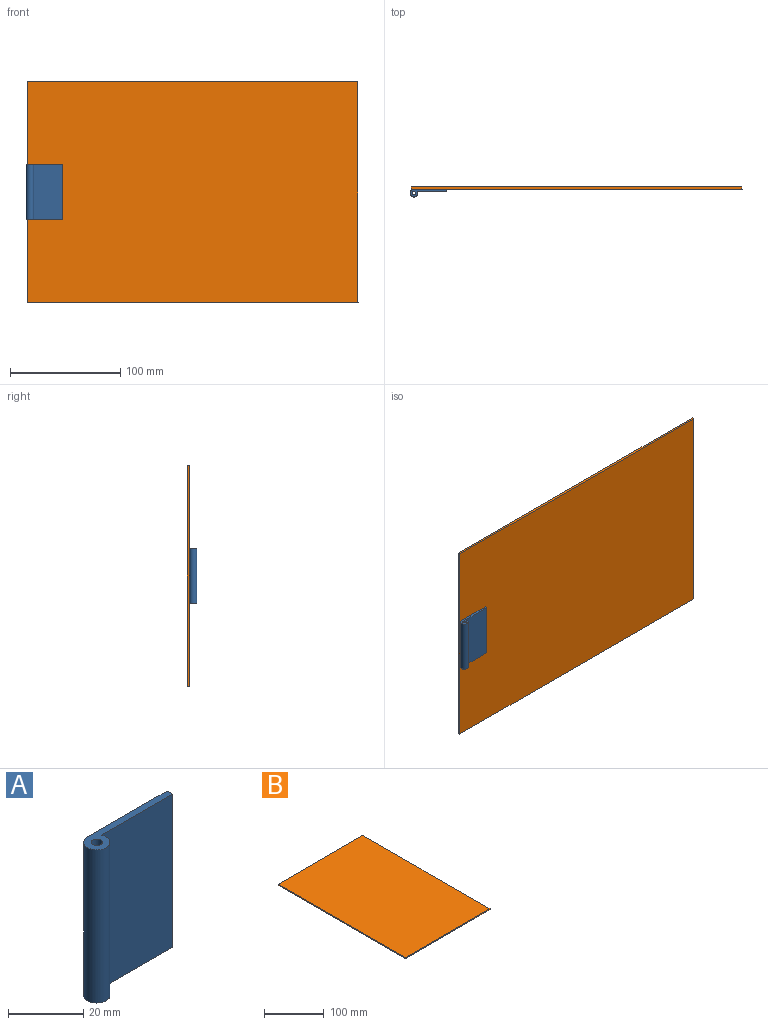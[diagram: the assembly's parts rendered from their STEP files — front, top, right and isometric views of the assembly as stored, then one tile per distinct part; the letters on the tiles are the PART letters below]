
ASSEMBLY  parts=2 mates=1
PART A: 7 faces, bbox 33.5x7x50 mm
  f0: plane 50x30mm, normal (0,1,0), area 1500mm2, adj f1,f4,f5,f6
  f1: cylinder r=3.5mm len=50mm, axis (0,0,-1), area 902.2mm2, adj f0,f2,f5,f6
  f2: plane 50x26.84mm, normal (0,-1,0), area 1341.9mm2, adj f1,f4,f5,f6
  f3: cylinder r=1.5mm len=50mm, axis (0,0,-1), area 471.2mm2, adj f5,f6
  f4: plane 50x2mm, normal (1,0,0), area 100mm2, adj f0,f2,f5,f6
  f5: plane 33.5x7mm, normal (0,0,1), area 86.9mm2, adj f0,f1,f2,f3,f4
  f6: plane 33.5x7mm, normal (0,0,-1), area 86.9mm2, adj f0,f1,f2,f3,f4
PART B: 6 faces, bbox 200x300x2 mm
  f0: plane 200x2mm, normal (0,1,0), area 400mm2, adj f1,f3,f4,f5
  f1: plane 300x2mm, normal (-1,0,0), area 600mm2, adj f0,f2,f4,f5
  f2: plane 200x2mm, normal (0,-1,0), area 400mm2, adj f1,f3,f4,f5
  f3: plane 300x2mm, normal (1,0,0), area 600mm2, adj f0,f2,f4,f5
  f4: plane 300x200mm, normal (0,0,1), area 60000mm2, adj f0,f1,f2,f3
  f5: plane 300x200mm, normal (0,0,-1), area 60000mm2, adj f0,f1,f2,f3
PLACE A t=(-142.08,226.11,-26.74)mm
PLACE B rot(axis=(0.58,-0.58,0.58),120deg) t=(154.06,13.6,-1.74)mm
MATE fastened B.f4 <-> A.f0  axis (0,-1,0) through (154.06,11.6,-1.74)mm
